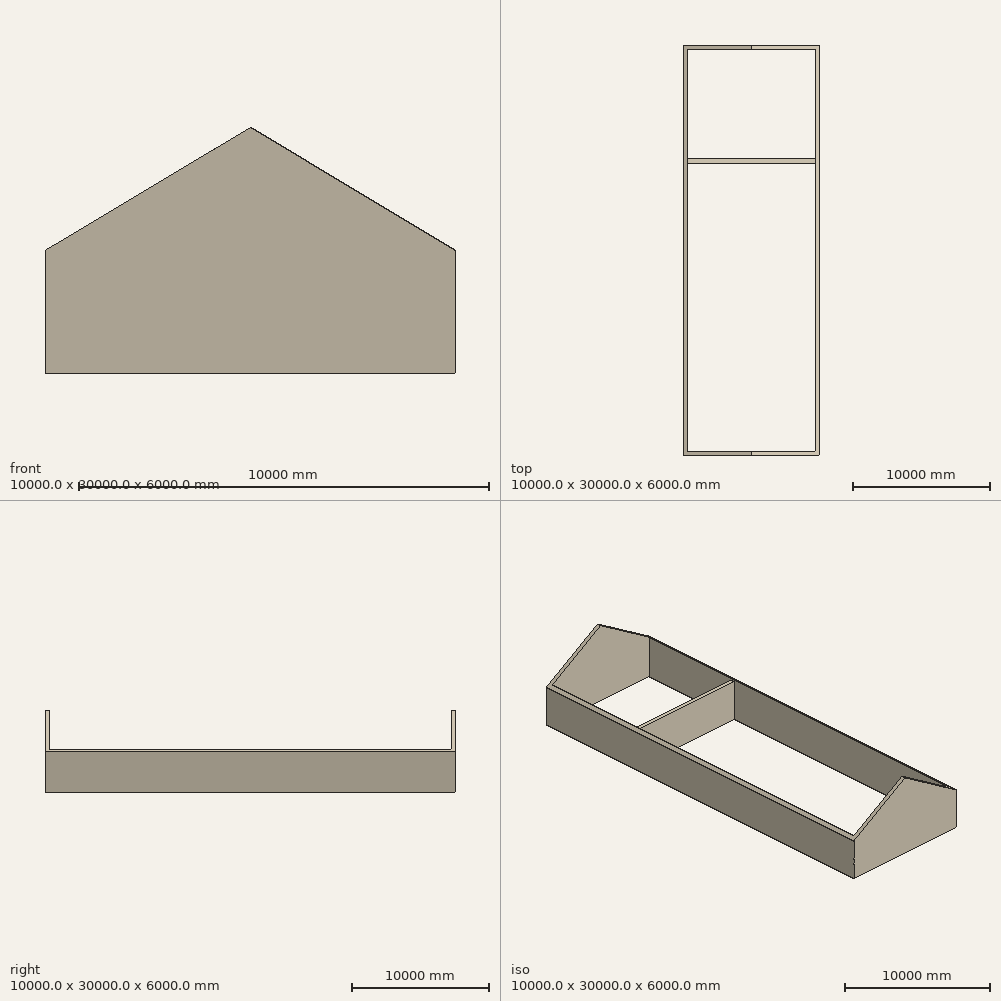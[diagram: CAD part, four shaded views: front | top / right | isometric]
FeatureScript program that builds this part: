
annotation { "Feature Type Name" : "Feature", "Feature Type Description" : "" }
export const myFeature = defineFeature(function(context is Context, id is Id, definition is map)
    precondition{}
    {
        {
            var Q0;
            Q0=qCreatedBy(makeId("Top.planeOp"),FACE);
            var sketch = newSketch(context, id + "F0", { "sketchPlane" : qUnion([Q0])});
            skLineSegment(sketch, "E0.bottom", {"start": v(-5010.47, 0) * mm, "end": v(4989.53, 0) * mm});
            skLineSegment(sketch, "E0.top", {"start": v(-5010.47, -30000) * mm, "end": v(4989.53, -30000) * mm});
            skLineSegment(sketch, "E0.left", {"start": v(-5010.47, 0) * mm, "end": v(-5010.47, -30000) * mm});
            skLineSegment(sketch, "E0.right", {"start": v(4989.53, 0) * mm, "end": v(4989.53, -30000) * mm});
            skLineSegment(sketch, "E1.bottom", {"start": v(-4710.47, -300) * mm, "end": v(4689.53, -300) * mm});
            skLineSegment(sketch, "E1.top", {"start": v(-4710.47, -29700) * mm, "end": v(4689.53, -29700) * mm});
            skLineSegment(sketch, "E1.left", {"start": v(-4710.47, -300) * mm, "end": v(-4710.47, -29700) * mm});
            skLineSegment(sketch, "E1.right", {"start": v(4689.53, -300) * mm, "end": v(4689.53, -29700) * mm});
            skLineSegment(sketch, "E2", {"start": v(-4710.47, -8300) * mm, "end": v(4689.53, -8300) * mm});
            skLineSegment(sketch, "E3", {"start": v(4689.53, -8300) * mm, "end": v(4689.53, -8600) * mm});
            skLineSegment(sketch, "E4", {"start": v(4689.53, -8600) * mm, "end": v(-4710.47, -8600) * mm});
            skSolve(sketch);
        }
        {
            var Q0;
            Q0 = qSketchRegion(id + "F0", true);
            extrude(context, id + "F1", {"entities" : qUnion([Q0]), "depth" : 6000 * mm});
        }
        {
            var Q0;
            {var subQ0=sQuery(id+"F0.wireOp",EDGE,"E2");Q0=makeQuery(id+"F0.imprint","IMPRINT",FACE,{"disambiguationData":[TD([[makeQuery(id+"F0.imprint","IMPRINT",EDGE,{"derivedFrom":subQ0}),-1.0]])]});}
            extrude(context, id + "F2", {"entities" : qUnion([Q0]), "operationType" : NewBodyOperationType.ADD, "depth" : 3000 * mm});
        }
        {
            var Q0;
            Q0=qCreatedBy(makeId("Front.planeOp"),FACE);
            var sketch = newSketch(context, id + "F3", { "sketchPlane" : qUnion([Q0])});
            skLineSegment(sketch, "E5", {"start": v(-5010.47, 3000) * mm, "end": v(0, 6000) * mm});
            skLineSegment(sketch, "E6", {"start": v(0, 6000) * mm, "end": v(4989.53, 3000) * mm});
            skLineSegment(sketch, "E7", {"start": v(-5010.47, 3000) * mm, "end": v(-5010.47, 6000) * mm});
            skLineSegment(sketch, "E8", {"start": v(-5010.47, 6000) * mm, "end": v(4989.53, 6000) * mm});
            skLineSegment(sketch, "E9", {"start": v(4989.53, 6000) * mm, "end": v(4989.53, 3000) * mm});
            skSolve(sketch);
        }
        {
            var Q0;
            Q0 = qSketchRegion(id + "F3", true);
            extrude(context, id + "F4", {"entities" : qUnion([Q0]), "operationType" : NewBodyOperationType.REMOVE, "oppositeDirection" : true, "depth" : 1000 * mm});
        }
        {
            var Q0;
            Q0 = qSketchRegion(id + "F3", true);
            extrude(context, id + "F5", {"entities" : qUnion([Q0]), "operationType" : NewBodyOperationType.REMOVE, "endBound" : BoundingType.THROUGH_ALL, "depth" : 1000 * mm});
        }
    });
